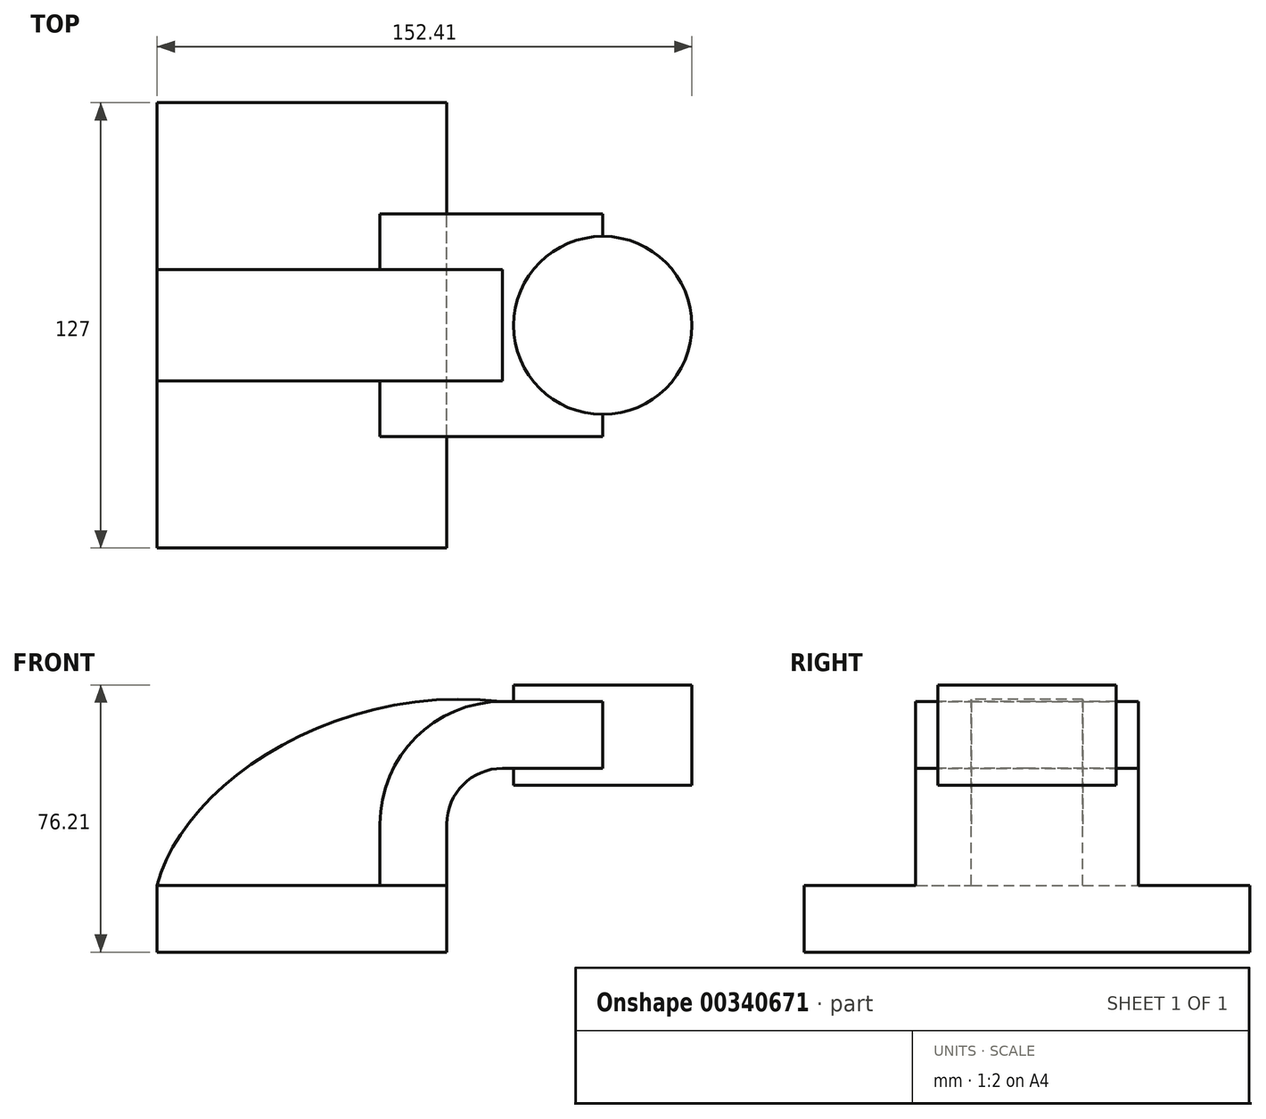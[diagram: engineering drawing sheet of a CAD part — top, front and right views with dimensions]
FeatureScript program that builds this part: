
annotation { "Feature Type Name" : "Feature", "Feature Type Description" : "" }
export const myFeature = defineFeature(function(context is Context, id is Id, definition is map)
    precondition{}
    {
        {
            var Q0;
            Q0=qCreatedBy(makeId("Front.planeOp"),FACE);
            var sketch = newSketch(context, id + "F0", { "sketchPlane" : qUnion([Q0])});
            skLineSegment(sketch, "E0.bottom", {"start": v(-41.28, 9.52) * mm, "end": v(41.28, 9.52) * mm});
            skLineSegment(sketch, "E0.top", {"start": v(-41.27, -9.53) * mm, "end": v(41.28, -9.53) * mm});
            skLineSegment(sketch, "E0.left", {"start": v(-41.28, 9.52) * mm, "end": v(-41.27, -9.53) * mm});
            skLineSegment(sketch, "E0.right", {"start": v(41.28, 9.52) * mm, "end": v(41.28, -9.52) * mm});
            skPoint(sketch, "E0.middle", {"position": v(0, 0) * mm});
            skLineSegment(sketch, "E1.bottom", {"start": v(60.32, 38.1) * mm, "end": v(111.12, 38.1) * mm});
            skLineSegment(sketch, "E1.top", {"start": v(60.32, 66.67) * mm, "end": v(111.12, 66.67) * mm});
            skLineSegment(sketch, "E1.left", {"start": v(60.32, 38.1) * mm, "end": v(60.32, 66.67) * mm});
            skLineSegment(sketch, "E1.right", {"start": v(111.12, 38.1) * mm, "end": v(111.12, 66.67) * mm});
            skPoint(sketch, "E1.middle", {"position": v(85.72, 52.39) * mm});
            skLineSegment(sketch, "E2", {"start": v(41.27, 9.53) * mm, "end": v(41.27, 27) * mm});
            skArc(sketch, "E3", {"start": v(57.15, 42.88) * mm, "mid": v(45.92, 38.23) * mm, "end": v(41.27, 27) * mm});
            skLineSegment(sketch, "E4", {"start": v(57.15, 42.88) * mm, "end": v(85.72, 42.88) * mm});
            skLineSegment(sketch, "E5.0", {"start": v(57.15, 61.93) * mm, "end": v(85.72, 61.93) * mm});
            skArc(sketch, "E5.1", {"start": v(57.15, 61.93) * mm, "mid": v(32.45, 51.7) * mm, "end": v(22.22, 27) * mm});
            skLineSegment(sketch, "E5.2", {"start": v(22.22, 9.53) * mm, "end": v(22.22, 27) * mm});
            skLineSegment(sketch, "E6", {"start": v(85.72, 61.93) * mm, "end": v(85.72, 42.88) * mm});
            skFitSpline(sketch, "E7", {"points": [v(-41.27, 9.53) * mm, v(57.15, 61.93) * mm], "startDerivative": vector(21, 82.98) * mm, "endDerivative": vector(147.88, -16.88) * mm});
            skLineSegment(sketch, "E8", {"start": v(85.72, 38.1) * mm, "end": v(85.72, 66.67) * mm});
            skSolve(sketch);
        }
        {
            var Q0;
            Q0=makeQuery(id+"F0.imprint","IMPRINT",FACE,{"disambiguationData":[TD([[makeQuery(id+"F0.imprint","IMPRINT",EDGE,{"derivedFrom":sQuery(id+"F0.wireOp",EDGE,"E0.top")}),1.0]])]});
            extrude(context, id + "F1", {"entities" : qUnion([Q0]), "endBound" : BoundingType.SYMMETRIC, "depth" : 127 * mm});
        }
        {
            var Q0;
            {var subQ1=sQuery(id+"F0.wireOp",EDGE,"E2");Q0=makeQuery(id+"F0.imprint","IMPRINT",FACE,{"disambiguationData":[TD([[makeQuery(id+"F0.imprint","IMPRINT",EDGE,{"derivedFrom":subQ1}),1.0]])]});}
            var Q1;
            {var subQ5=sQuery(id+"F0.wireOp",EDGE,"E6");Q1=makeQuery(id+"F0.imprint","IMPRINT",FACE,{"disambiguationData":[TD([[makeQuery(id+"F0.imprint","IMPRINT",EDGE,{"derivedFrom":subQ5}),-1.0]])]});}
            var Q2;
            {var subQ0=sQuery(id+"F0.wireOp",EDGE,"E4");var subQ1=sQuery(id+"F0.wireOp",EDGE,"E1.left");var subQ2=makeQuery(id+"F0.imprint","INTERSECT",VERTEX,{"derivedFrom":[subQ1,subQ0]});Q2=makeQuery(id+"F0.imprint","IMPRINT",FACE,{"disambiguationData":[TD([[makeQuery(id+"F0.imprint","IMPRINT",EDGE,{"disambiguationData":[TD([[subQ2,-1.0]])],"derivedFrom":subQ1}),-1.0]])]});}
            extrude(context, id + "F2", {"entities" : qUnion([Q0, Q1, Q2]), "operationType" : NewBodyOperationType.ADD, "endBound" : BoundingType.SYMMETRIC, "depth" : 63.5 * mm});
        }
        {
            var Q0;
            {var subQ4=sQuery(id+"F0.wireOp",EDGE,"E1.right");Q0=makeQuery(id+"F0.imprint","IMPRINT",FACE,{"disambiguationData":[TD([[makeQuery(id+"F0.imprint","IMPRINT",EDGE,{"derivedFrom":subQ4}),1.0]])]});}
            var Q1;
            Q1=sQuery(id+"F0.wireOp",EDGE,"E8");
            revolve(context, id + "F3", {"operationType" : NewBodyOperationType.ADD, "entities" : qUnion([Q0]), "axis" : qUnion([Q1]), "revolveType" : RevolveType.FULL});
        }
        {
            var Q0;
            Q0=makeQuery(id+"F0.imprint","IMPRINT",FACE,{"disambiguationData":[TD([[makeQuery(id+"F0.imprint","IMPRINT",EDGE,{"derivedFrom":sQuery(id+"F0.wireOp",EDGE,"E5.1")}),-1.0]])]});
            extrude(context, id + "F4", {"entities" : qUnion([Q0]), "operationType" : NewBodyOperationType.ADD, "endBound" : BoundingType.SYMMETRIC, "depth" : 31.75 * mm});
        }
    });
